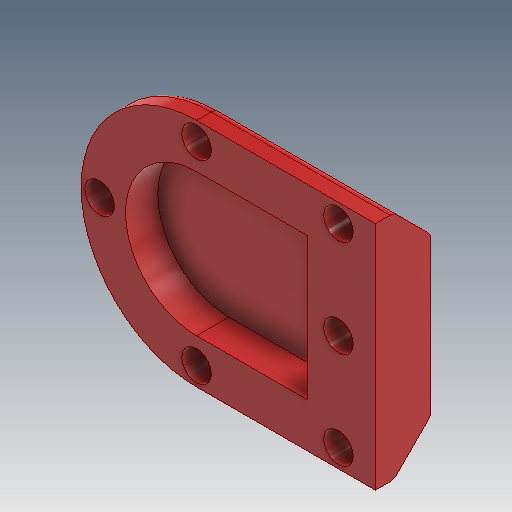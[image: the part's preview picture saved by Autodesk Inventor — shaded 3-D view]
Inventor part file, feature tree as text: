
AUTODESK INVENTOR PART (.ipt)
format: ipt  version: 2020.3 (Build 243373010, 373A)  size: 217,088 bytes
history: native  units: mm
features: sketch x2, extrude x2, fillet x2, chamfer x1, projected_geometry x1
ambient origin geometry x8: Origin, YZ Plane, XZ Plane, XY Plane, X Axis, Y Axis, Z Axis, Center Point
bodies: Body1 (feature_tree)
feature tree (8):
  sketch  "Sketch6"  dims[d37=60.0mm d42=16.05mm]
  extrude  "Extrusion8"  Depth=16.05mm
  chamfer  "Chamfer3"  Distance=38.5mm
  fillet  "Fillet3"  Radius=30.0mm
  extrude  "Extrusion10"  Depth=5.0mm TaperAngle=45.0deg
  fillet  "Fillet4"  Radius=5.0mm
  sketch  "Sketch7"  dims[d43=60.0mm d44=38.5mm d45=30.0mm d46=0.0mm d49=20.0mm d50=2.0mm d51=45.0deg d52=5.0mm d53=12.5mm d54=0.0mm d55=5.0mm]
  projected_geometry  "Projected Loop5"
